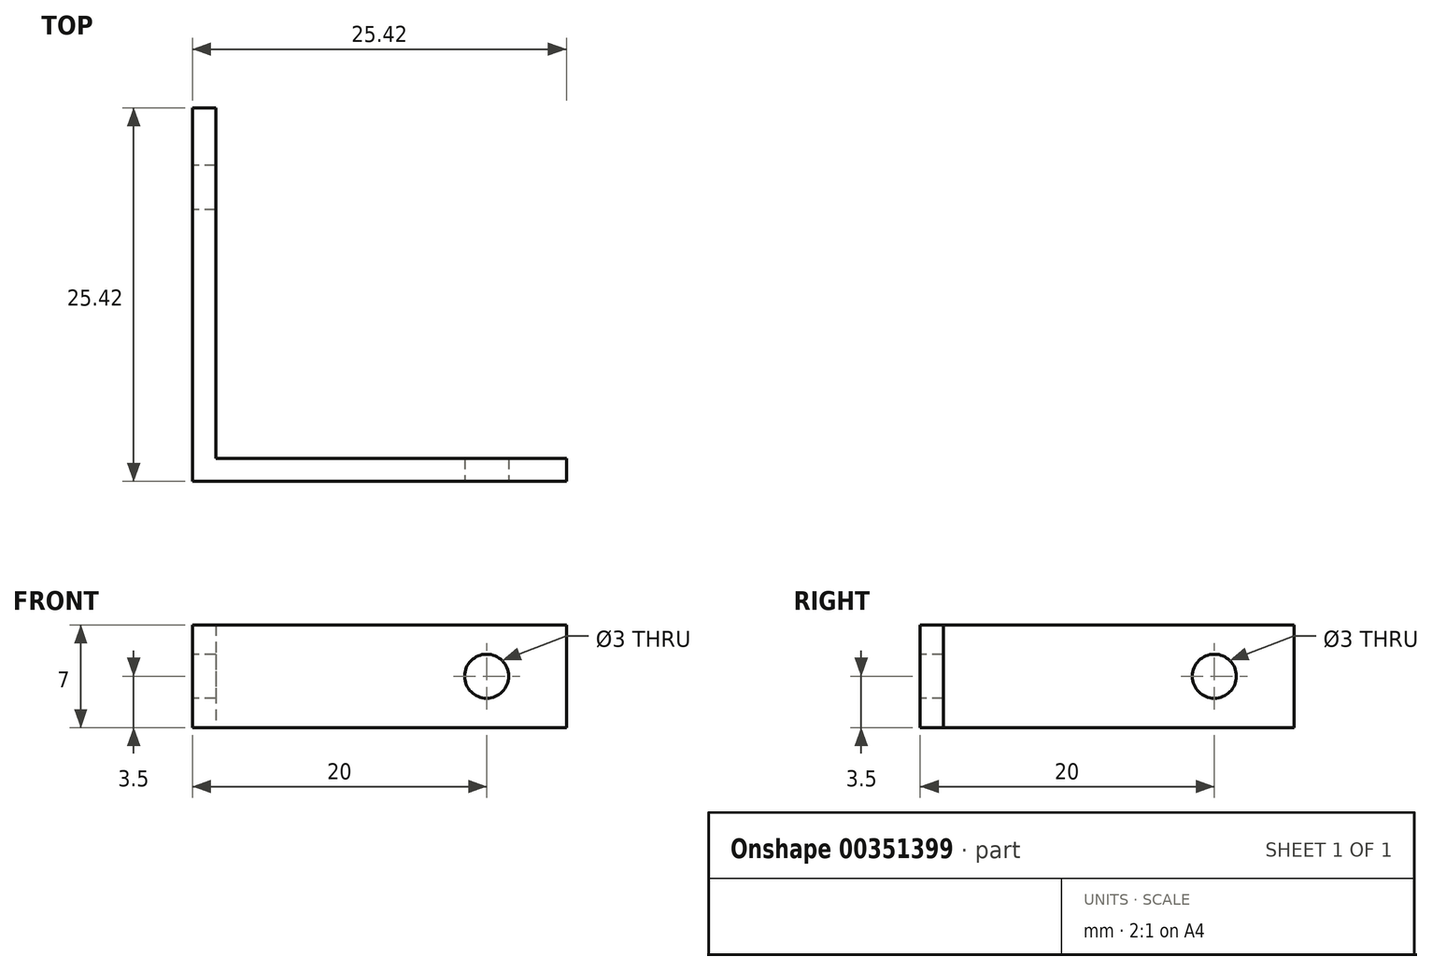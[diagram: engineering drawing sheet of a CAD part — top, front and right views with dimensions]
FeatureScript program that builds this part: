
annotation { "Feature Type Name" : "Feature", "Feature Type Description" : "" }
export const myFeature = defineFeature(function(context is Context, id is Id, definition is map)
    precondition{}
    {
        {
            var Q0;
            Q0=qCreatedBy(makeId("Top.planeOp"),FACE);
            var sketch = newSketch(context, id + "F0", { "sketchPlane" : qUnion([Q0])});
            skLineSegment(sketch, "E0.bottom", {"start": v(0, 0) * mm, "end": v(1.58, 0) * mm});
            skLineSegment(sketch, "E0.top", {"start": v(0, 25.42) * mm, "end": v(1.58, 25.42) * mm});
            skLineSegment(sketch, "E0.left", {"start": v(0, 0) * mm, "end": v(0, 25.42) * mm});
            skLineSegment(sketch, "E0.right", {"start": v(1.58, 0) * mm, "end": v(1.58, 25.42) * mm});
            skLineSegment(sketch, "E1.bottom", {"start": v(1.58, 0) * mm, "end": v(25.42, 0) * mm});
            skLineSegment(sketch, "E1.top", {"start": v(1.58, 1.58) * mm, "end": v(25.42, 1.58) * mm});
            skLineSegment(sketch, "E1.left", {"start": v(1.58, 0) * mm, "end": v(1.58, 1.58) * mm});
            skLineSegment(sketch, "E1.right", {"start": v(25.42, 0) * mm, "end": v(25.42, 1.58) * mm});
            skSolve(sketch);
        }
        {
            var Q0;
            Q0 = qSketchRegion(id + "F0", true);
            extrude(context, id + "F1", {"entities" : qUnion([Q0]), "depth" : 7 * mm});
        }
        {
            var Q0;
            Q0=makeQuery(id+"F1.opExtrude","SWEPT_FACE",FACE,{"disambiguationData":[OSD([sQuery(id+"F0.wireOp",EDGE,"E0.left")])]});
            var sketch = newSketch(context, id + "F2", { "sketchPlane" : qUnion([Q0])});
            skCircle(sketch, "E2", {"center": v(-20, 3.5) * mm, "radius": 1.5 * mm});
            skSolve(sketch);
        }
        {
            var Q0;
            Q0 = qSketchRegion(id + "F2", true);
            extrude(context, id + "F3", {"entities" : qUnion([Q0]), "operationType" : NewBodyOperationType.REMOVE, "oppositeDirection" : true, "depth" : 25 * mm});
        }
        {
            var Q0;
            Q0=makeQuery(id+"F1.opExtrude","SWEPT_FACE",FACE,{"disambiguationData":[OSD([sQuery(id+"F0.wireOp",EDGE,"E0.bottom"),sQuery(id+"F0.wireOp",EDGE,"E1.bottom")])]});
            var sketch = newSketch(context, id + "F4", { "sketchPlane" : qUnion([Q0])});
            skCircle(sketch, "E3", {"center": v(20, 3.5) * mm, "radius": 1.5 * mm});
            skSolve(sketch);
        }
        {
            var Q0;
            Q0 = qSketchRegion(id + "F4", true);
            extrude(context, id + "F5", {"entities" : qUnion([Q0]), "operationType" : NewBodyOperationType.REMOVE, "oppositeDirection" : true, "depth" : 25 * mm});
        }
    });
